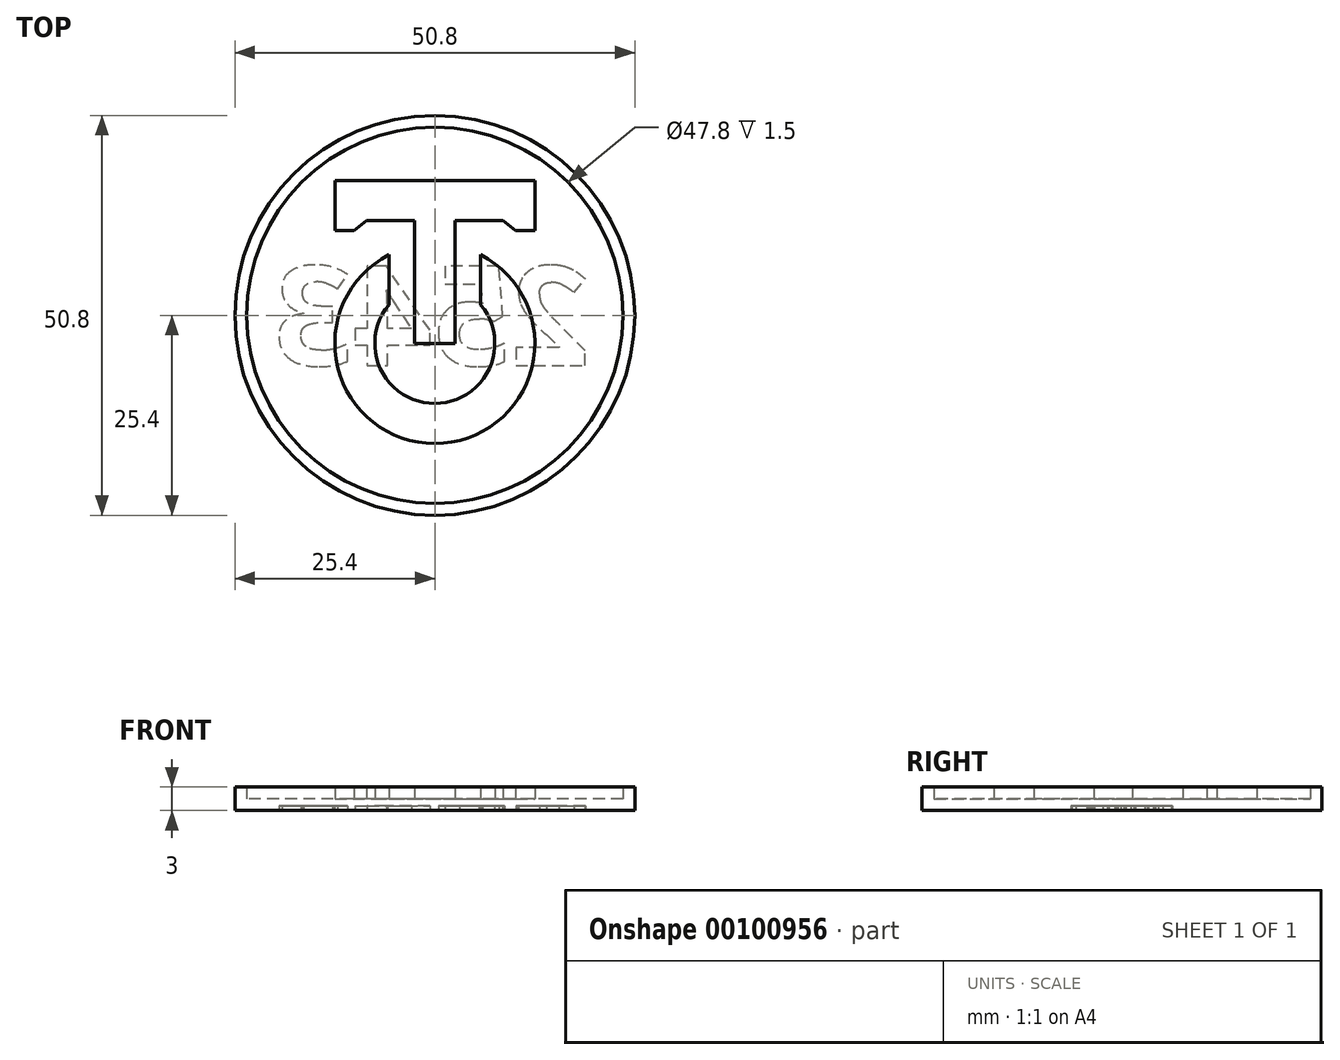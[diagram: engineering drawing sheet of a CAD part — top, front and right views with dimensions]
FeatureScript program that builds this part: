
annotation { "Feature Type Name" : "Feature", "Feature Type Description" : "" }
export const myFeature = defineFeature(function(context is Context, id is Id, definition is map)
    precondition{}
    {
        {
            var Q0;
            Q0=qCreatedBy(makeId("Top.planeOp"),FACE);
            var sketch = newSketch(context, id + "F0", { "sketchPlane" : qUnion([Q0])});
            skCircle(sketch, "E0", {"center": v(0, 0) * mm, "radius": 25.4 * mm});
            skSolve(sketch);
        }
        {
            var Q0;
            Q0=makeQuery(id+"F0.imprint","IMPRINT",FACE,{"disambiguationData":[TD([[makeQuery(id+"F0.imprint","IMPRINT",EDGE,{"derivedFrom":sQuery(id+"F0.wireOp",EDGE,"E0")}),1.0]])]});
            extrude(context, id + "F1", {"entities" : qUnion([Q0]), "depth" : 1.5 * mm});
        }
        {
            var Q0;
            Q0=makeQuery(id+"F1.opExtrude","CAP_FACE",FACE,{"disambiguationData":[OSD([sQuery(id+"F0.wireOp",EDGE,"E0")])],"isStart":false});
            var sketch = newSketch(context, id + "F2", { "sketchPlane" : qUnion([Q0])});
            skCircle(sketch, "E1.0", {"center": v(0, 0) * mm, "radius": 25.4 * mm});
            skCircle(sketch, "E2.0", {"center": v(0, 0) * mm, "radius": 23.9 * mm});
            skSolve(sketch);
        }
        {
            var Q0;
            Q0=makeQuery(id+"F2.imprint","IMPRINT",FACE,{"disambiguationData":[TD([[makeQuery(id+"F2.imprint","IMPRINT",EDGE,{"derivedFrom":sQuery(id+"F2.wireOp",EDGE,"E1.0")}),1.0]])]});
            extrude(context, id + "F3", {"entities" : qUnion([Q0]), "operationType" : NewBodyOperationType.ADD, "depth" : 1.5 * mm});
        }
        {
            var Q0;
            Q0=makeQuery(id+"F1.opExtrude","CAP_FACE",FACE,{"disambiguationData":[OSD([sQuery(id+"F0.wireOp",EDGE,"E0")])],"isStart":false});
            var sketch = newSketch(context, id + "F4", { "sketchPlane" : qUnion([Q0])});
            skArc(sketch, "E3", {"start": v(-5.84, 7.7) * mm, "mid": v(0, -16.28) * mm, "end": v(5.84, 7.7) * mm});
            skArc(sketch, "E4", {"start": v(-5.84, 1.31) * mm, "mid": v(0, -11.2) * mm, "end": v(5.84, 1.31) * mm});
            skLineSegment(sketch, "E5", {"start": v(-5.84, 1.31) * mm, "end": v(-5.84, 7.7) * mm});
            skLineSegment(sketch, "E6", {"start": v(0, 0) * mm, "end": v(0, 41.24) * mm, "construction": true});
            skLineSegment(sketch, "E7.MirrorCS", {"start": v(5.84, 1.31) * mm, "end": v(5.84, 7.7) * mm});
            skLineSegment(sketch, "E8", {"start": v(0, -3.58) * mm, "end": v(2.54, -3.58) * mm});
            skLineSegment(sketch, "E9", {"start": v(2.54, -3.58) * mm, "end": v(2.54, 12.01) * mm});
            skLineSegment(sketch, "E10", {"start": v(2.54, 12.01) * mm, "end": v(8.7, 12.01) * mm});
            skLineSegment(sketch, "E11", {"start": v(8.7, 12.01) * mm, "end": v(10.24, 10.74) * mm});
            skLineSegment(sketch, "E12", {"start": v(10.24, 10.74) * mm, "end": v(12.7, 10.74) * mm});
            skLineSegment(sketch, "E13", {"start": v(12.7, 10.74) * mm, "end": v(12.7, 17.1) * mm});
            skLineSegment(sketch, "E14", {"start": v(12.7, 17.1) * mm, "end": v(0, 17.1) * mm});
            skLineSegment(sketch, "E15.MirrorCS", {"start": v(-2.54, -3.58) * mm, "end": v(-2.54, 12.01) * mm});
            skLineSegment(sketch, "E16.MirrorCS", {"start": v(0, -3.58) * mm, "end": v(-2.54, -3.58) * mm});
            skLineSegment(sketch, "E17.MirrorCS", {"start": v(-2.54, 12.01) * mm, "end": v(-8.7, 12.01) * mm});
            skLineSegment(sketch, "E18.MirrorCS", {"start": v(-12.7, 17.1) * mm, "end": v(0, 17.1) * mm});
            skLineSegment(sketch, "E19.MirrorCS", {"start": v(-12.7, 10.74) * mm, "end": v(-12.7, 17.1) * mm});
            skLineSegment(sketch, "E20.MirrorCS", {"start": v(-10.24, 10.74) * mm, "end": v(-12.7, 10.74) * mm});
            skLineSegment(sketch, "E21.MirrorCS", {"start": v(-8.7, 12.01) * mm, "end": v(-10.24, 10.74) * mm});
            skSolve(sketch);
        }
        {
            var Q0;
            Q0=makeQuery(id+"F4.imprint","IMPRINT",FACE,{"disambiguationData":[TD([[makeQuery(id+"F4.imprint","IMPRINT",EDGE,{"derivedFrom":sQuery(id+"F4.wireOp",EDGE,"E3")}),1.0]])]});
            var Q1;
            Q1=makeQuery(id+"F4.imprint","IMPRINT",FACE,{"disambiguationData":[TD([[makeQuery(id+"F4.imprint","IMPRINT",EDGE,{"derivedFrom":sQuery(id+"F4.wireOp",EDGE,"E8")}),1.0]])]});
            extrude(context, id + "F5", {"entities" : qUnion([Q0, Q1]), "operationType" : NewBodyOperationType.ADD, "depth" : 1.5 * mm});
        }
        {
            var Q0;
            Q0=makeQuery(id+"F1.opExtrude","CAP_FACE",FACE,{"disambiguationData":[OSD([sQuery(id+"F0.wireOp",EDGE,"E0")])],"isStart":true});
            var sketch = newSketch(context, id + "F6", { "sketchPlane" : qUnion([Q0])});
            skText(sketch, "E22", { "text": "2543", "fontName": "OpenSans-Bold.ttf"});
            const initialGuessF6  = {"E22": [0.0198, 0.00635, -1, 0, 0.0127]};
            skSetInitialGuess(sketch, initialGuessF6);
            skSolve(sketch);
        }
        {
            var Q0;
            Q0=makeQuery(id+"F6.imprint","IMPRINT",FACE,{"disambiguationData":[TD([[makeQuery(id+"F6.imprint","IMPRINT",EDGE,{"derivedFrom":sQuery(id+"F6.wireOp",EDGE,"E22.sketch_text.stroke-0")}),-1.0]])]});
            var Q1;
            Q1=makeQuery(id+"F6.imprint","IMPRINT",FACE,{"disambiguationData":[TD([[makeQuery(id+"F6.imprint","IMPRINT",EDGE,{"derivedFrom":sQuery(id+"F6.wireOp",EDGE,"E22.sketch_text.stroke-24")}),-1.0]])]});
            var Q2;
            Q2=makeQuery(id+"F6.imprint","IMPRINT",FACE,{"disambiguationData":[TD([[makeQuery(id+"F6.imprint","IMPRINT",EDGE,{"derivedFrom":sQuery(id+"F6.wireOp",EDGE,"E22.sketch_text.stroke-44")}),-1.0]])]});
            var Q3;
            Q3=makeQuery(id+"F6.imprint","IMPRINT",FACE,{"disambiguationData":[TD([[makeQuery(id+"F6.imprint","IMPRINT",EDGE,{"derivedFrom":sQuery(id+"F6.wireOp",EDGE,"E22.sketch_text.stroke-62")}),-1.0]])]});
            extrude(context, id + "F7", {"entities" : qUnion([Q0, Q1, Q2, Q3]), "operationType" : NewBodyOperationType.REMOVE, "oppositeDirection" : true, "depth" : .6 * mm});
        }
    });
